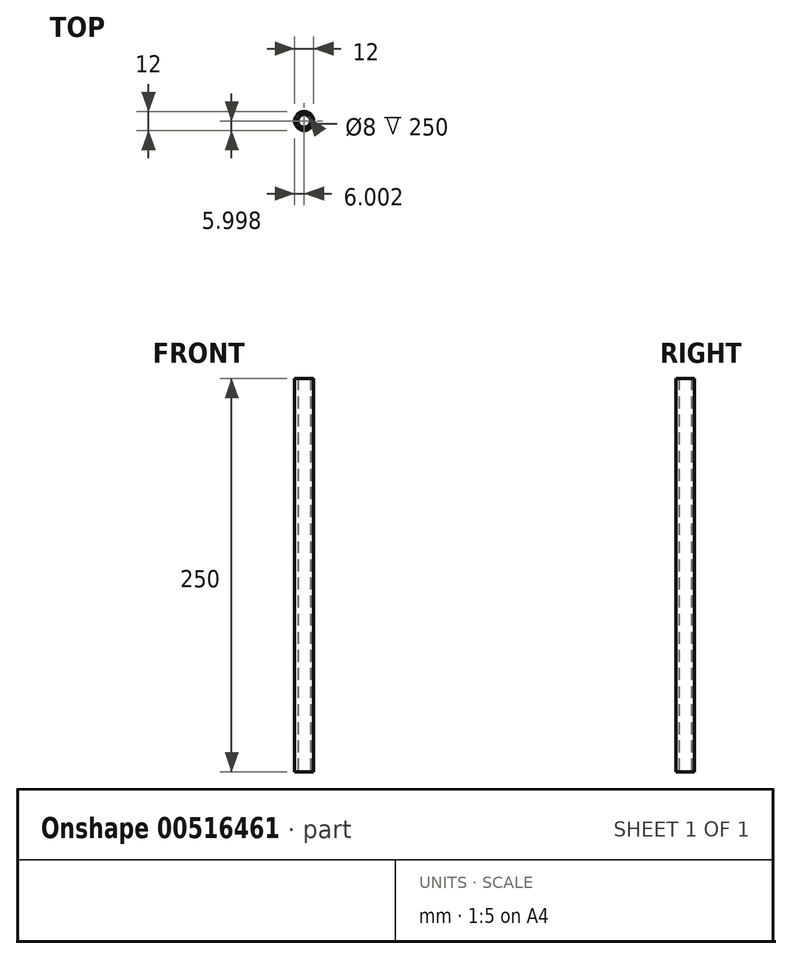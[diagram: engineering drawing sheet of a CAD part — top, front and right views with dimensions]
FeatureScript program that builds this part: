
annotation { "Feature Type Name" : "Feature", "Feature Type Description" : "" }
export const myFeature = defineFeature(function(context is Context, id is Id, definition is map)
    precondition{}
    {
        {
            var Q0;
            Q0=qCreatedBy(makeId("Top.planeOp"),FACE);
            var sketch = newSketch(context, id + "F0", { "sketchPlane" : qUnion([Q0])});
            skCircle(sketch, "E0", {"center": v(-11.07, -8.47) * mm, "radius": 6 * mm});
            skCircle(sketch, "E1.0", {"center": v(-11.07, -8.47) * mm, "radius": 4 * mm});
            skSolve(sketch);
        }
        {
            var Q0;
            Q0=makeQuery(id+"F0.imprint","IMPRINT",FACE,{"disambiguationData":[TD([[makeQuery(id+"F0.imprint","IMPRINT",EDGE,{"derivedFrom":sQuery(id+"F0.wireOp",EDGE,"E0")}),1.0]])]});
            extrude(context, id + "F1", {"entities" : qUnion([Q0]), "depth" : 250 * mm, "offsetDistance" : 25 * mm});
        }
    });
